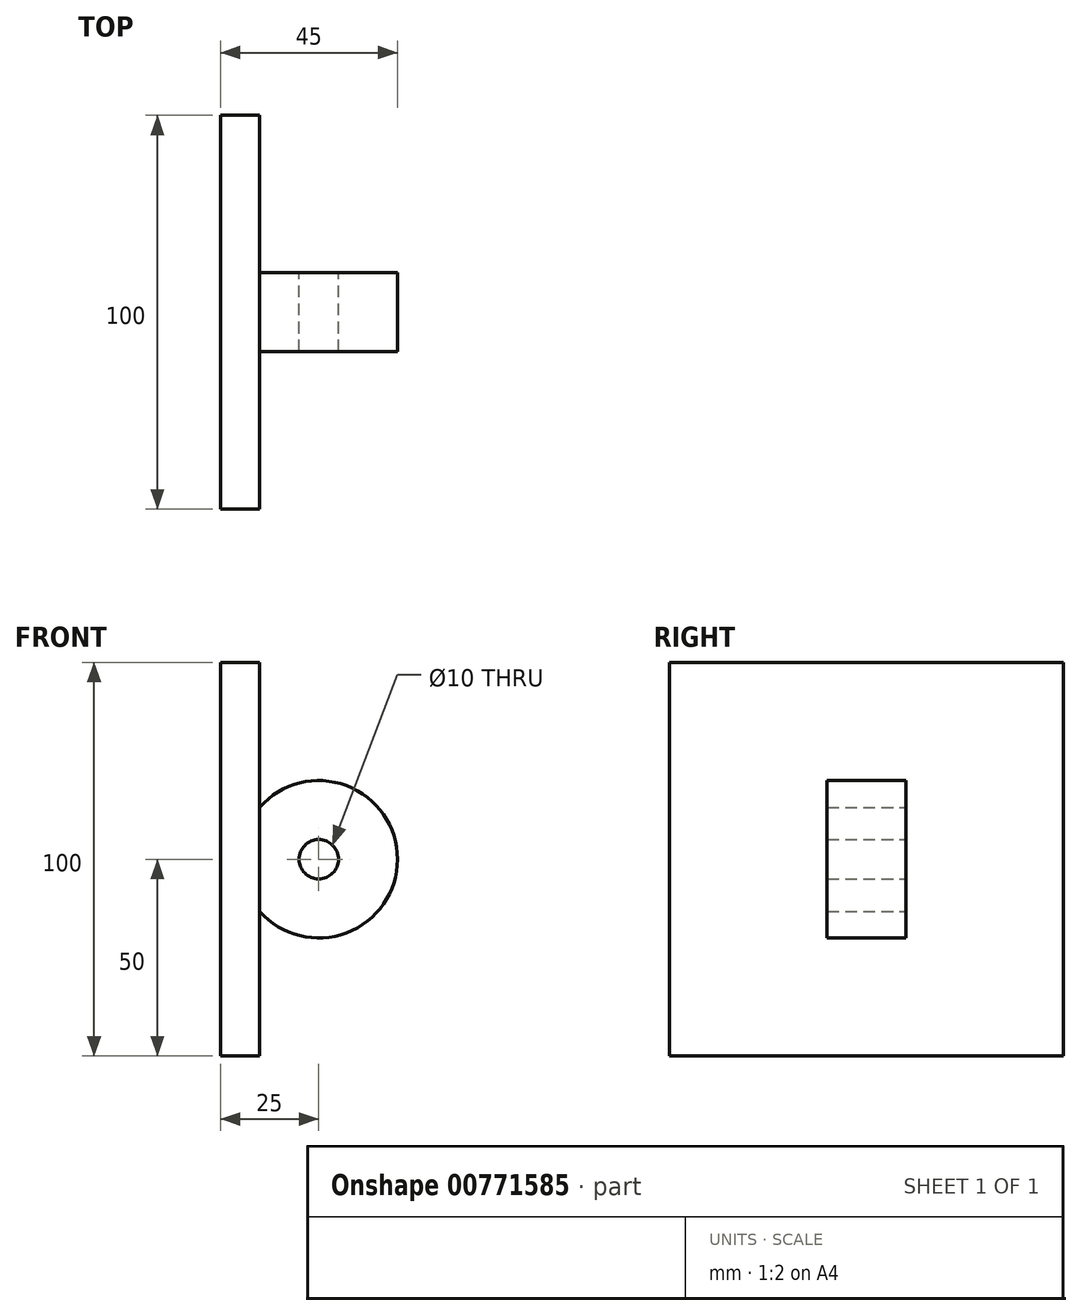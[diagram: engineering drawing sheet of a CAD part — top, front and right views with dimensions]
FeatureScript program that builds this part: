
annotation { "Feature Type Name" : "Feature", "Feature Type Description" : "" }
export const myFeature = defineFeature(function(context is Context, id is Id, definition is map)
    precondition{}
    {
        {
            var Q0;
            Q0=qCreatedBy(makeId("Right.planeOp"),FACE);
            var sketch = newSketch(context, id + "F0", { "sketchPlane" : qUnion([Q0])});
            skLineSegment(sketch, "E0.bottom", {"start": v(50, -50) * mm, "end": v(-50, -50) * mm});
            skLineSegment(sketch, "E0.top", {"start": v(50, 50) * mm, "end": v(-50, 50) * mm});
            skLineSegment(sketch, "E0.left", {"start": v(50, -50) * mm, "end": v(50, 50) * mm});
            skLineSegment(sketch, "E0.right", {"start": v(-50, -50) * mm, "end": v(-50, 50) * mm});
            skPoint(sketch, "E0.middle", {"position": v(0, 0) * mm});
            skSolve(sketch);
        }
        {
            var Q0;
            Q0=makeQuery(id+"F0.imprint","IMPRINT",FACE,{"disambiguationData":[TD([[makeQuery(id+"F0.imprint","IMPRINT",EDGE,{"derivedFrom":sQuery(id+"F0.wireOp",EDGE,"E0.bottom")}),-1.0]])]});
            extrude(context, id + "F1", {"entities" : qUnion([Q0]), "depth" : 10 * mm, "offsetDistance" : 25 * mm});
        }
        {
            var Q0;
            Q0=makeQuery(id+"F1.opExtrude","CAP_FACE",FACE,{"disambiguationData":[OSD([sQuery(id+"F0.wireOp",EDGE,"E0.bottom"),sQuery(id+"F0.wireOp",EDGE,"E0.top"),sQuery(id+"F0.wireOp",EDGE,"E0.left"),sQuery(id+"F0.wireOp",EDGE,"E0.right")])],"isStart":false});
            var sketch = newSketch(context, id + "F2", { "sketchPlane" : qUnion([Q0])});
            skLineSegment(sketch, "E1.bottom", {"start": v(10, 35) * mm, "end": v(-10, 35) * mm});
            skLineSegment(sketch, "E1.top", {"start": v(10, -35) * mm, "end": v(-10, -35) * mm});
            skLineSegment(sketch, "E1.left", {"start": v(10, 35) * mm, "end": v(10, -35) * mm});
            skLineSegment(sketch, "E1.right", {"start": v(-10, 35) * mm, "end": v(-10, -35) * mm});
            skPoint(sketch, "E1.middle", {"position": v(0, 0) * mm});
            skSolve(sketch);
        }
        {
            var Q0;
            Q0=makeQuery(id+"F2.imprint","IMPRINT",FACE,{"disambiguationData":[TD([[makeQuery(id+"F2.imprint","IMPRINT",EDGE,{"derivedFrom":sQuery(id+"F2.wireOp",EDGE,"E1.bottom")}),1.0]])]});
            extrude(context, id + "F3", {"entities" : qUnion([Q0]), "operationType" : NewBodyOperationType.ADD, "depth" : 70 * mm, "offsetDistance" : 25 * mm});
        }
        {
            var Q0;
            Q0=makeQuery(id+"F3.opExtrude","SWEPT_FACE",FACE,{"disambiguationData":[OSD([sQuery(id+"F2.wireOp",EDGE,"E1.left")])]});
            var sketch = newSketch(context, id + "F4", { "sketchPlane" : qUnion([Q0])});
            skPoint(sketch, "E2", {"position": v(-25, 0) * mm});
            skArc(sketch, "E3", {"start": v(-10, 13.23) * mm, "mid": v(-45, 0) * mm, "end": v(-10, -13.23) * mm});
            skCircle(sketch, "E4", {"center": v(-25, 0) * mm, "radius": 5 * mm});
            skSolve(sketch);
        }
        {
            var Q0;
            {var subQ1=sQuery(id+"F2.wireOp",EDGE,"E1.left");var subQ6=makeQuery(id+"F3.opExtrude","CAP_EDGE",EDGE,{"disambiguationData":[OSD([subQ1])],"isStart":false});Q0=makeQuery(id+"F4.imprint","IMPRINT",FACE,{"disambiguationData":[TD([[makeQuery(id+"F4.imprint","IMPRINT",EDGE,{"derivedFrom":subQ6}),1.0]])]});}
            var Q1;
            {var subQ0=sQuery(id+"F4.wireOp",EDGE,"E3");var subQ1=sQuery(id+"F2.wireOp",EDGE,"E1.left");var subQ2=makeQuery(id+"F3.opExtrude","CAP_EDGE",EDGE,{"disambiguationData":[OSD([subQ1])],"isStart":true});var subQ3=makeQuery(id+"F4.imprint","INTERSECT",VERTEX,{"disambiguationData":[OD(0.0)],"derivedFrom":[subQ2,subQ0]});Q1=makeQuery(id+"F4.imprint","IMPRINT",FACE,{"disambiguationData":[TD([[makeQuery(id+"F4.imprint","IMPRINT",EDGE,{"disambiguationData":[TD([[subQ3,-1.0]])],"derivedFrom":subQ0}),-1.0]])]});}
            var Q2;
            {var subQ0=sQuery(id+"F4.wireOp",EDGE,"E3");var subQ1=sQuery(id+"F2.wireOp",EDGE,"E1.left");var subQ2=makeQuery(id+"F3.opExtrude","CAP_EDGE",EDGE,{"disambiguationData":[OSD([subQ1])],"isStart":true});var subQ3=makeQuery(id+"F4.imprint","INTERSECT",VERTEX,{"disambiguationData":[OD(1.0)],"derivedFrom":[subQ2,subQ0]});Q2=makeQuery(id+"F4.imprint","IMPRINT",FACE,{"disambiguationData":[TD([[makeQuery(id+"F4.imprint","IMPRINT",EDGE,{"disambiguationData":[TD([[subQ3,1.0]])],"derivedFrom":subQ0}),-1.0]])]});}
            extrude(context, id + "F5", {"entities" : qUnion([Q0, Q1, Q2]), "operationType" : NewBodyOperationType.REMOVE, "endBound" : BoundingType.THROUGH_ALL, "oppositeDirection" : true, "depth" : 25 * mm, "offsetDistance" : 25 * mm});
        }
        {
            var Q0;
            Q0=makeQuery(id+"F4.imprint","IMPRINT",FACE,{"disambiguationData":[TD([[makeQuery(id+"F4.imprint","IMPRINT",EDGE,{"derivedFrom":sQuery(id+"F4.wireOp",EDGE,"E4")}),1.0]])]});
            extrude(context, id + "F6", {"entities" : qUnion([Q0]), "operationType" : NewBodyOperationType.REMOVE, "endBound" : BoundingType.THROUGH_ALL, "oppositeDirection" : true, "depth" : 25 * mm, "offsetDistance" : 25 * mm});
        }
    });
